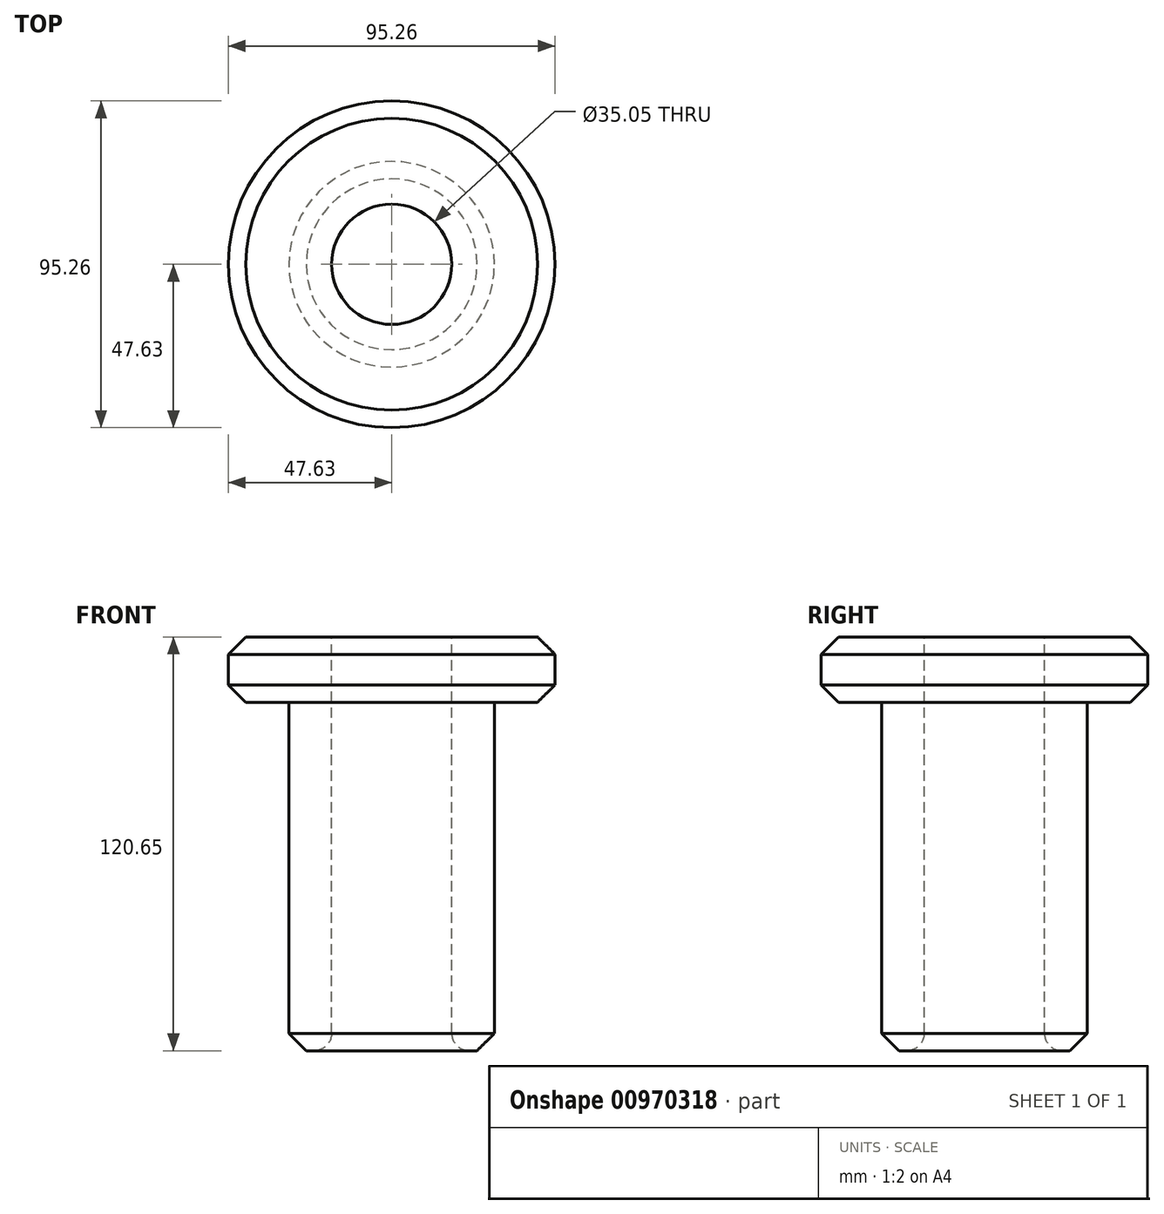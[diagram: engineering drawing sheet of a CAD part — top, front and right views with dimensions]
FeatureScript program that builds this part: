
annotation { "Feature Type Name" : "Feature", "Feature Type Description" : "" }
export const myFeature = defineFeature(function(context is Context, id is Id, definition is map)
    precondition{}
    {
        {
            var Q0;
            Q0=qCreatedBy(makeId("Top.planeOp"),FACE);
            var sketch = newSketch(context, id + "F0", { "sketchPlane" : qUnion([Q0])});
            skCircle(sketch, "E0", {"center": v(0, 0) * mm, "radius": 29.97 * mm});
            skSolve(sketch);
        }
        {
            var Q0;
            Q0 = qSketchRegion(id + "F0", true);
            extrude(context, id + "F1", {"entities" : qUnion([Q0]), "oppositeDirection" : true, "depth" : 101.6 * mm, "offsetDistance" : 25.4 * mm});
        }
        {
            var Q0;
            Q0=qCreatedBy(makeId("Top.planeOp"),FACE);
            var sketch = newSketch(context, id + "F2", { "sketchPlane" : qUnion([Q0])});
            skCircle(sketch, "E1", {"center": v(0, 0) * mm, "radius": 47.63 * mm});
            skSolve(sketch);
        }
        {
            var Q0;
            Q0 = qSketchRegion(id + "F2", true);
            extrude(context, id + "F3", {"entities" : qUnion([Q0]), "operationType" : NewBodyOperationType.ADD, "depth" : 19.05 * mm, "offsetDistance" : 25.4 * mm});
        }
        {
            var Q0;
            Q0=makeQuery(id+"F3.opExtrude","CAP_FACE",FACE,{"disambiguationData":[OSD([sQuery(id+"F2.wireOp",EDGE,"E1")])],"isStart":false});
            var sketch = newSketch(context, id + "F4", { "sketchPlane" : qUnion([Q0])});
            skCircle(sketch, "E2", {"center": v(0, 0) * mm, "radius": 17.53 * mm});
            skSolve(sketch);
        }
        {
            var Q0;
            Q0 = qSketchRegion(id + "F4", true);
            extrude(context, id + "F5", {"entities" : qUnion([Q0]), "operationType" : NewBodyOperationType.REMOVE, "endBound" : BoundingType.THROUGH_ALL, "oppositeDirection" : true, "depth" : 25.4 * mm, "offsetDistance" : 25.4 * mm});
        }
        {
            var Q0;
            Q0=makeQuery(id+"F1.opExtrude","CAP_EDGE",EDGE,{"disambiguationData":[OSD([sQuery(id+"F0.wireOp",EDGE,"E0")])],"isStart":false});
            var Q1;
            Q1=makeQuery(id+"F3.opExtrude","CAP_EDGE",EDGE,{"disambiguationData":[OSD([sQuery(id+"F2.wireOp",EDGE,"E1")])],"isStart":true});
            var Q2;
            Q2=makeQuery(id+"F3.opExtrude","CAP_EDGE",EDGE,{"disambiguationData":[OSD([sQuery(id+"F2.wireOp",EDGE,"E1")])],"isStart":false});
            chamfer(context, id + "F6", {"entities" : qUnion([Q0, Q1, Q2]), "width" : 5.08 * mm, "tangentPropagation" : true});
        }
        {
            var Q0;
            Q0=makeQuery(id+"F5.boolean.opBoolean","COPY",EDGE,{"derivedFrom":makeQuery(id+"F5.opExtrude","CAP_EDGE",EDGE,{"disambiguationData":[OSD([sQuery(id+"F4.wireOp",EDGE,"E2")])],"isStart":true})});
            var Q1;
            Q1=makeQuery(id+"F5.boolean.opBoolean","INTERSECT",EDGE,{"derivedFrom":[makeQuery(id+"F1.opExtrude","CAP_FACE",FACE,{"disambiguationData":[OSD([sQuery(id+"F0.wireOp",EDGE,"E0")])],"isStart":false}),makeQuery(id+"F5.opExtrude","SWEPT_FACE",FACE,{"disambiguationData":[OSD([sQuery(id+"F4.wireOp",EDGE,"E2")])]})]});
            fillet(context, id + "F7", {"entities" : qUnion([Q0, Q1]), "radius" : 5.08 * mm, "tangentPropagation" : true, "allowEdgeOverflow" : false});
        }
    });
